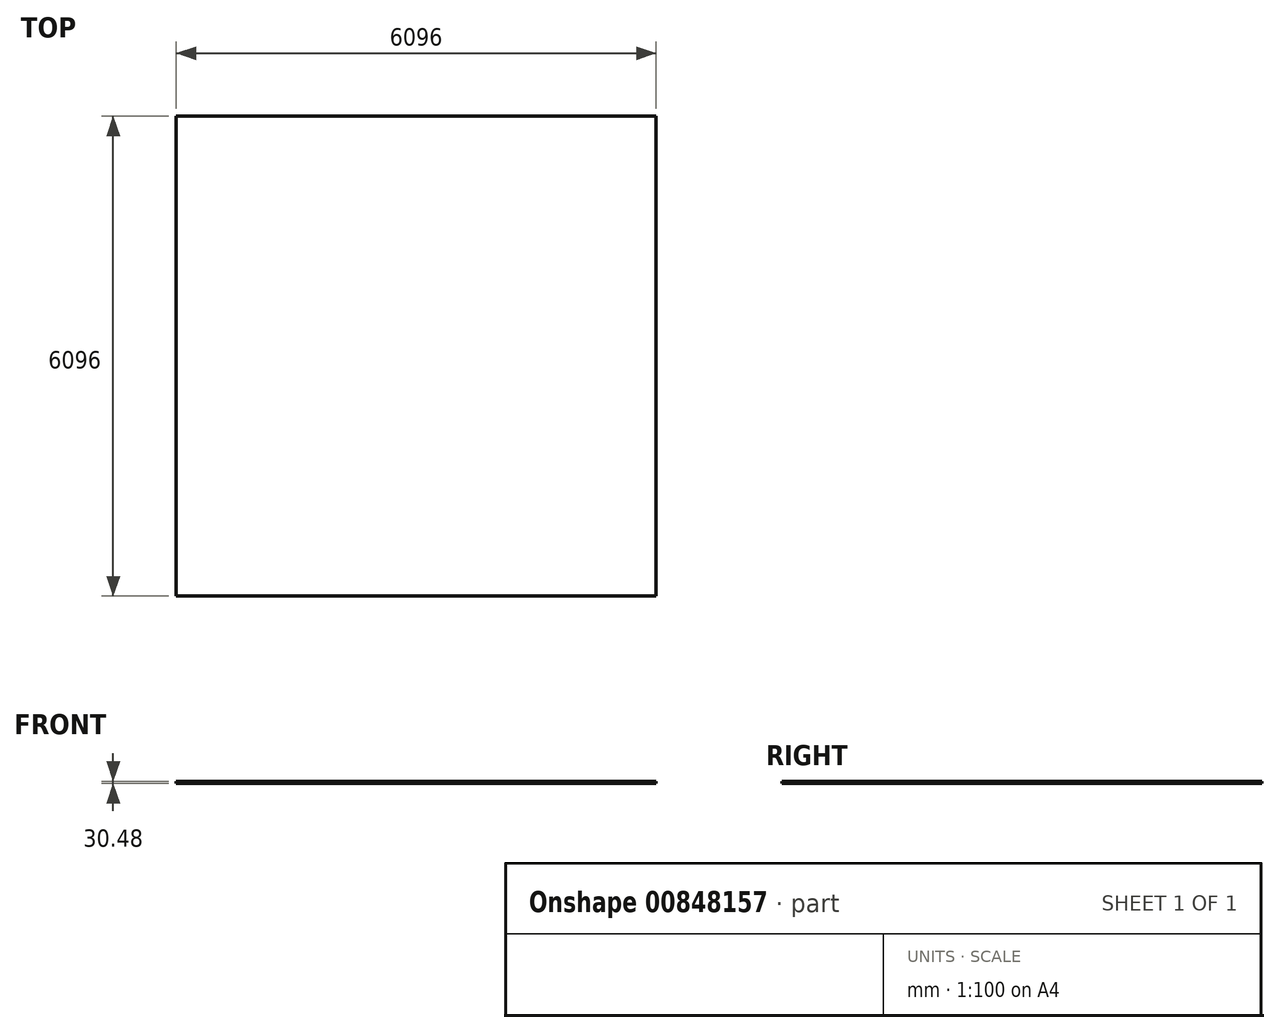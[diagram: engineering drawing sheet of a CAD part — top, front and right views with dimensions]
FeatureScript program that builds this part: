
annotation { "Feature Type Name" : "Feature", "Feature Type Description" : "" }
export const myFeature = defineFeature(function(context is Context, id is Id, definition is map)
    precondition{}
    {
        {
            var Q0;
            Q0=qCreatedBy(makeId("Top.planeOp"),FACE);
            var sketch = newSketch(context, id + "F0", { "sketchPlane" : qUnion([Q0])});
            skLineSegment(sketch, "E0.bottom", {"start": v(-3048, 3048) * mm, "end": v(3048, 3048) * mm});
            skLineSegment(sketch, "E0.top", {"start": v(-3048, -3048) * mm, "end": v(3048, -3048) * mm});
            skLineSegment(sketch, "E0.left", {"start": v(-3048, 3048) * mm, "end": v(-3048, -3048) * mm});
            skLineSegment(sketch, "E0.right", {"start": v(3048, 3048) * mm, "end": v(3048, -3048) * mm});
            skPoint(sketch, "E0.middle", {"position": v(0, 0) * mm});
            skSolve(sketch);
        }
        {
            var Q0;
            Q0 = qSketchRegion(id + "F0", true);
            extrude(context, id + "F1", {"entities" : qUnion([Q0]), "depth" : 30.48 * mm, "offsetDistance" : 30.48 * mm});
        }
    });
